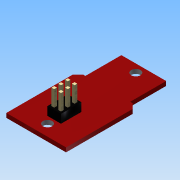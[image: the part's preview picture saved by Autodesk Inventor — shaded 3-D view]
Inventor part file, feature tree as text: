
AUTODESK INVENTOR PART (.ipt)
format: ipt  version: 2015 (Build 190159000, 159)  size: 171,008 bytes
history: native  units: in
note: dims shown in document units (in); Inventor stores cm internally (conversion verified against a paired STEP export)
features: sketch x5, extrude x4, hole x1, pattern_linear x1
ambient origin geometry x8: Origin, YZ Plane, XZ Plane, XY Plane, X Axis, Y Axis, Z Axis, Center Point
bodies: Solid1 (feature_tree)
feature tree (11):
  extrude  "Extrusion1"  Depth=1.055in
  hole  "Hole1"  [1 undecoded]
  extrude  "Extrusion2"  Depth=0.075in
  extrude  "Extrusion3"  Depth=0.075in
  pattern_linear  "Rectangular Pattern1"  Spacing1=0.167in  [1 undecoded]
  extrude  "Extrusion4"  Depth=0.065in
  sketch  "Sketch1"  dims[d0=0.88in d1=1.055in]
  sketch  "Sketch2"  dims[d2=0.66in d3=0.53in]
  sketch  "Sketch3"  dims[d4=0.075in d5=0.075in]
  sketch  "Sketch4"  dims[d6=0.075in d7=0.075in]
  sketch  "Sketch5"  dims[d8=0.063in d9=0.0in d10=0.167in d11=0.117in d12=90.0deg d13=0.136in d14=0.75in d15=0.252in d16=0.25in d17=0.5635in d18=1.0in d19=0.8108in d20=90.0deg d21=90.0deg d22=0.415in d23=0.2in d24=0.3in d25=0.125in d26=0.0in d27=0.04in d28=0.04in d29=0.06in d30=0.16in d31=0.236in d32=0.0in d33=0.7874in d35=0.1in d36=1.1811in d38=0.1in d39=0.105in d40=0.132in d41=0.34in d42=0.59in d43=0.34in d44=0.065in d45=0.0in]
note: 2 required parameter values undecoded (feature->parameter linkage not recoverable at this tier; creation-order binding heuristic only, values carry confidence <= 0.55)
